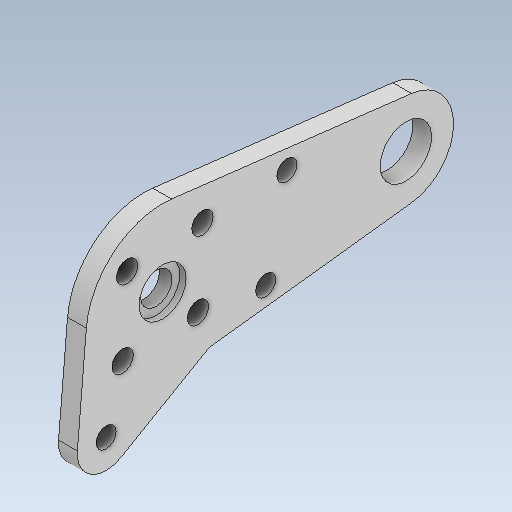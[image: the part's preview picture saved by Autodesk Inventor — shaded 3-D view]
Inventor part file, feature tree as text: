
AUTODESK INVENTOR PART (.ipt)
format: ipt  version: 2020 (Build 240168000, 168)  size: 260,608 bytes
history: native  units: mm
features: extrude x5, sketch x4, projected_geometry x3
ambient origin geometry x8: Origin, YZ Plane, XZ Plane, XY Plane, X Axis, Y Axis, Z Axis, Center Point
bodies: Body1 (feature_tree)
feature tree (12):
  extrude  "Выдавливание4"  Depth=18.6mm
  extrude  "Выдавливание5"  Depth=12.2mm
  extrude  "Выдавливание6"  Depth=9.7mm
  extrude  "Выдавливание7"  Depth=7.1mm
  extrude  "Выдавливание8"  Depth=38.82013mm
  sketch  "Эскиз4"
  projected_geometry  "Спроецированная петля3"
  sketch  "Эскиз5"
  sketch  "Эскиз6"
  projected_geometry  "Спроецированная петля4"
  sketch  "Эскиз7"
  projected_geometry  "Спроецированная петля5"
